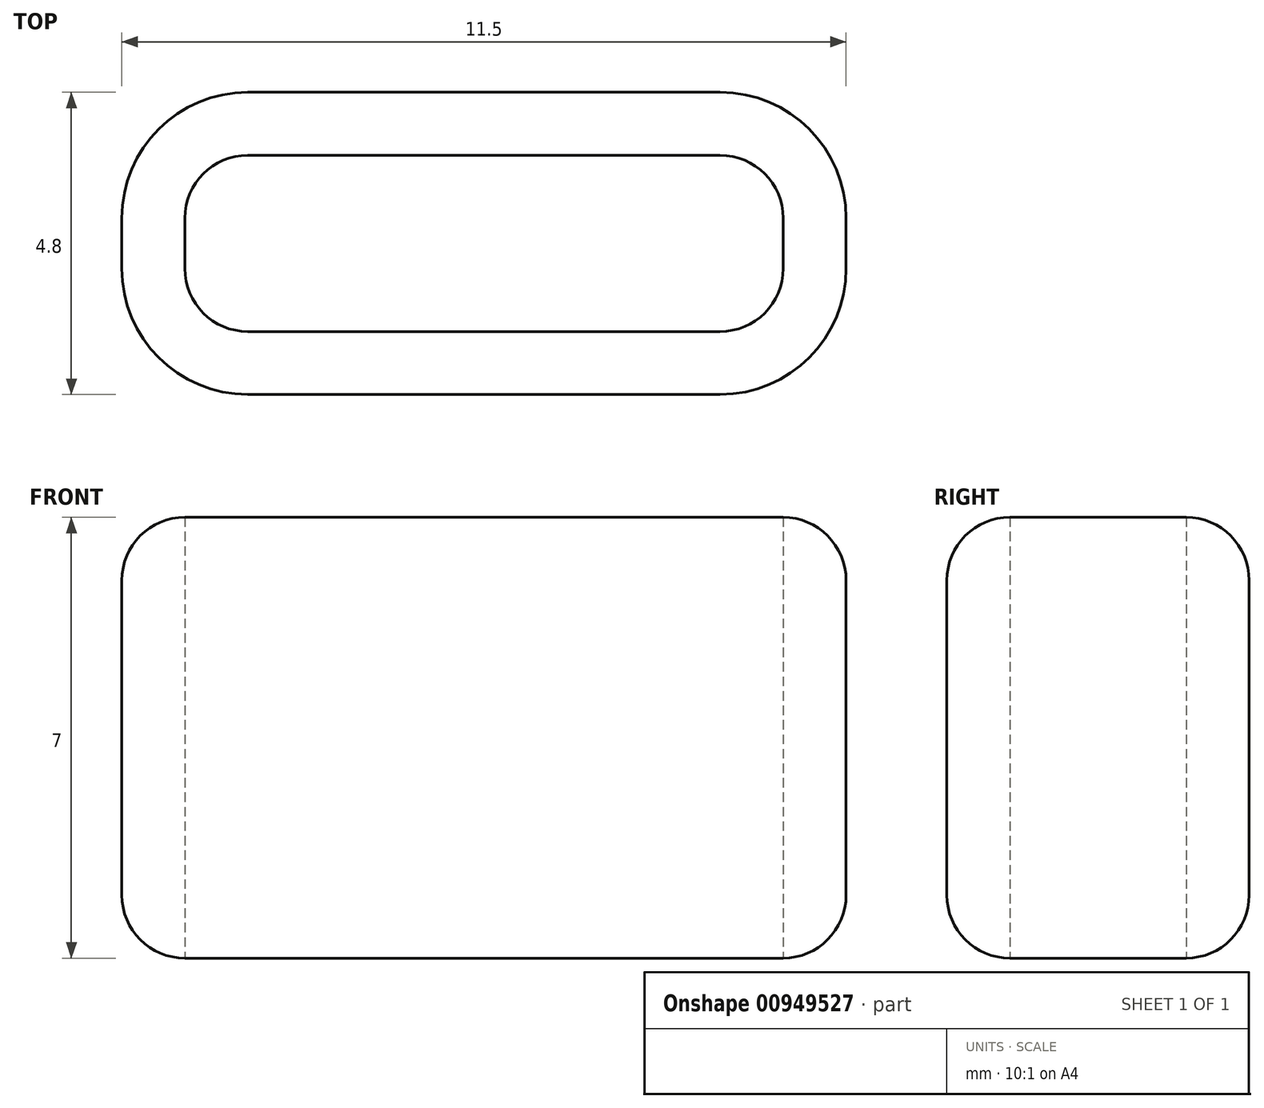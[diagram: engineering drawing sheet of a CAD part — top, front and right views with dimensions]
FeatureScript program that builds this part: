
annotation { "Feature Type Name" : "Feature", "Feature Type Description" : "" }
export const myFeature = defineFeature(function(context is Context, id is Id, definition is map)
    precondition{}
    {
        {
            var Q0;
            Q0=qCreatedBy(makeId("Top.planeOp"),FACE);
            var sketch = newSketch(context, id + "F0", { "sketchPlane" : qUnion([Q0])});
            skLineSegment(sketch, "E0.bottom", {"start": v(3.75, -1.4) * mm, "end": v(-3.75, -1.4) * mm});
            skLineSegment(sketch, "E0.top", {"start": v(3.75, 1.4) * mm, "end": v(-3.75, 1.4) * mm});
            skLineSegment(sketch, "E0.left", {"start": v(4.75, -0.4) * mm, "end": v(4.75, 0.4) * mm});
            skLineSegment(sketch, "E0.right", {"start": v(-4.75, -0.4) * mm, "end": v(-4.75, 0.4) * mm});
            skPoint(sketch, "E1.visualSharp", {"position": v(-4.75, 1.4) * mm});
            skArc(sketch, "E1.filletArc", {"start": v(-3.75, 1.4) * mm, "mid": v(-4.46, 1.1) * mm, "end": v(-4.75, 0.4) * mm});
            skPoint(sketch, "E2.visualSharp", {"position": v(4.75, 1.4) * mm});
            skArc(sketch, "E2.filletArc", {"start": v(4.75, 0.4) * mm, "mid": v(4.46, 1.1) * mm, "end": v(3.75, 1.4) * mm});
            skPoint(sketch, "E3.visualSharp", {"position": v(4.75, -1.4) * mm});
            skArc(sketch, "E3.filletArc", {"start": v(3.75, -1.4) * mm, "mid": v(4.46, -1.1) * mm, "end": v(4.75, -0.4) * mm});
            skPoint(sketch, "E4.visualSharp", {"position": v(-4.75, -1.4) * mm});
            skArc(sketch, "E4.filletArc", {"start": v(-4.75, -0.4) * mm, "mid": v(-4.46, -1.1) * mm, "end": v(-3.75, -1.4) * mm});
            skLineSegment(sketch, "E5.0", {"start": v(3.75, -2.4) * mm, "end": v(-3.75, -2.4) * mm});
            skArc(sketch, "E5.1", {"start": v(-5.75, -0.4) * mm, "mid": v(-5.16, -1.81) * mm, "end": v(-3.75, -2.4) * mm});
            skArc(sketch, "E5.2", {"start": v(3.75, -2.4) * mm, "mid": v(5.16, -1.81) * mm, "end": v(5.75, -0.4) * mm});
            skLineSegment(sketch, "E5.3", {"start": v(-5.75, -0.4) * mm, "end": v(-5.75, 0.4) * mm});
            skLineSegment(sketch, "E5.4", {"start": v(5.75, -0.4) * mm, "end": v(5.75, 0.4) * mm});
            skArc(sketch, "E5.5", {"start": v(5.75, 0.4) * mm, "mid": v(5.16, 1.81) * mm, "end": v(3.75, 2.4) * mm});
            skLineSegment(sketch, "E5.6", {"start": v(3.75, 2.4) * mm, "end": v(-3.75, 2.4) * mm});
            skArc(sketch, "E5.7", {"start": v(-3.75, 2.4) * mm, "mid": v(-5.16, 1.81) * mm, "end": v(-5.75, 0.4) * mm});
            skSolve(sketch);
        }
        {
            var Q0;
            Q0=makeQuery(id+"F0.imprint","IMPRINT",FACE,{"disambiguationData":[TD([[makeQuery(id+"F0.imprint","IMPRINT",EDGE,{"derivedFrom":sQuery(id+"F0.wireOp",EDGE,"E0.bottom")}),1.0]])]});
            extrude(context, id + "F1", {"entities" : qUnion([Q0]), "depth" : 7 * mm, "offsetDistance" : 25 * mm});
        }
        {
            var Q0;
            Q0=makeQuery(id+"F1.opExtrude","CAP_EDGE",EDGE,{"disambiguationData":[OSD([sQuery(id+"F0.wireOp",EDGE,"E5.6")])],"isStart":false});
            var Q1;
            Q1=makeQuery(id+"F1.opExtrude","CAP_EDGE",EDGE,{"disambiguationData":[OSD([sQuery(id+"F0.wireOp",EDGE,"E5.6")])],"isStart":true});
            fillet(context, id + "F2", {"entities" : qUnion([Q0, Q1]), "radius" : 1 * mm, "tangentPropagation" : true, "allowEdgeOverflow" : false});
        }
    });
